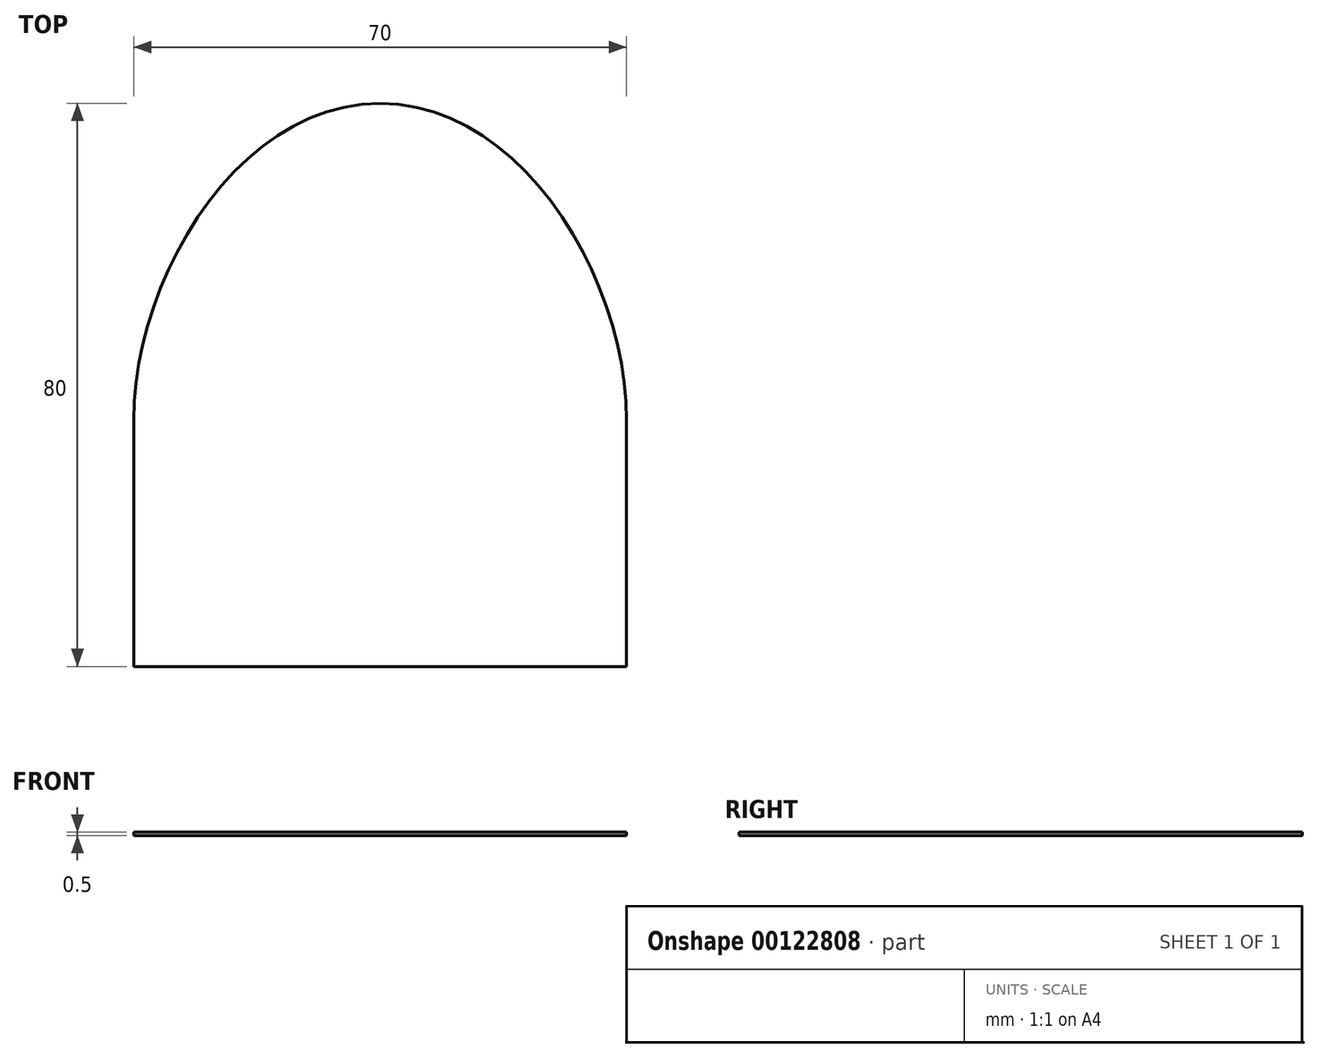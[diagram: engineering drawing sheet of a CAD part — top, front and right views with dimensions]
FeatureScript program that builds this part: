
annotation { "Feature Type Name" : "Feature", "Feature Type Description" : "" }
export const myFeature = defineFeature(function(context is Context, id is Id, definition is map)
    precondition{}
    {
        {
            var Q0;
            Q0=qCreatedBy(makeId("Top.planeOp"),FACE);
            var sketch = newSketch(context, id + "F0", { "sketchPlane" : qUnion([Q0])});
            skLineSegment(sketch, "E0.top", {"start": v(-35, -35) * mm, "end": v(35, -35) * mm});
            skPoint(sketch, "E0.middle", {"position": v(0, 13.14) * mm});
            skPoint(sketch, "E1", {"position": v(0, 0) * mm});
            skCircle(sketch, "E2", {"center": v(0, 0) * mm, "radius": 35 * mm});
            skPoint(sketch, "E3.visualSharp", {"position": v(-35, -35) * mm});
            skPoint(sketch, "E4.visualSharp", {"position": v(35, -35) * mm});
            skPoint(sketch, "E5", {"position": v(-35, 0) * mm});
            skPoint(sketch, "E6", {"position": v(35, 0) * mm});
            skFitSpline(sketch, "E7", {"points": [v(0, 45) * mm, v(-35, 0) * mm], "startDerivative": vector(-60.6, 0) * mm, "endDerivative": vector(0, -60.15) * mm});
            skLineSegment(sketch, "E8", {"start": v(-35, 0) * mm, "end": v(-35, -35) * mm});
            skLineSegment(sketch, "E9", {"start": v(35, 0) * mm, "end": v(35, -35) * mm});
            skFitSpline(sketch, "E10.MirrorCS", {"points": [v(0, 45) * mm, v(35, 0) * mm], "startDerivative": vector(60.6, 0) * mm, "endDerivative": vector(0, -60.15) * mm});
            skFitSpline(sketch, "E11.0", {"points": [v(0, 37) * mm, v(-0.85, 37) * mm, v(-2.51, 36.87) * mm, v(-4.95, 36.3) * mm, v(-7.36, 35.37) * mm, v(-10.54, 33.64) * mm, v(-14.42, 30.55) * mm, v(-18.67, 25.54) * mm, v(-22.24, 19.56) * mm, v(-24.95, 13) * mm, v(-26.62, 6.3) * mm, v(-27, 2.01) * mm, v(-27, 0) * mm]});
            skPoint(sketch, "E12", {"position": v(0, 37) * mm});
            skPoint(sketch, "E13", {"position": v(-7.77, 35.11) * mm});
            skPoint(sketch, "E14", {"position": v(-14.26, 30.43) * mm});
            skPoint(sketch, "E15", {"position": v(-19.34, 24.24) * mm});
            skPoint(sketch, "E16", {"position": v(-23.15, 17.21) * mm});
            skPoint(sketch, "E17", {"position": v(-25.74, 9.64) * mm});
            skLineSegment(sketch, "E18", {"start": v(-27, 0) * mm, "end": v(-27, -35) * mm});
            skPoint(sketch, "E19", {"position": v(-26.96, 1.74) * mm});
            skPoint(sketch, "E20", {"position": v(-27, -6.26) * mm});
            skPoint(sketch, "E21", {"position": v(-27, -14.26) * mm});
            skPoint(sketch, "E22", {"position": v(-27, -22.26) * mm});
            skPoint(sketch, "E23", {"position": v(-27, -30.26) * mm});
            skLineSegment(sketch, "E24.MirrorCS", {"start": v(27, 0) * mm, "end": v(27, -35) * mm});
            skPoint(sketch, "E25.MirrorP", {"position": v(7.77, 35.11) * mm});
            skPoint(sketch, "E26.MirrorP", {"position": v(14.26, 30.43) * mm});
            skPoint(sketch, "E27.MirrorP", {"position": v(19.34, 24.24) * mm});
            skPoint(sketch, "E28.MirrorP", {"position": v(23.15, 17.21) * mm});
            skPoint(sketch, "E29.MirrorP", {"position": v(25.74, 9.64) * mm});
            skPoint(sketch, "E30.MirrorP", {"position": v(26.96, 1.74) * mm});
            skPoint(sketch, "E31.MirrorP", {"position": v(27, -6.26) * mm});
            skPoint(sketch, "E32.MirrorP", {"position": v(27, -14.26) * mm});
            skPoint(sketch, "E33.MirrorP", {"position": v(27, -22.26) * mm});
            skPoint(sketch, "E34.MirrorP", {"position": v(27, -30.26) * mm});
            skFitSpline(sketch, "E35.0", {"points": [v(0, 37) * mm, v(0.85, 37) * mm, v(2.51, 36.87) * mm, v(4.95, 36.3) * mm, v(7.36, 35.37) * mm, v(10.54, 33.64) * mm, v(14.42, 30.55) * mm, v(18.67, 25.54) * mm, v(22.24, 19.56) * mm, v(24.95, 13) * mm, v(26.62, 6.3) * mm, v(27, 2.01) * mm, v(27, 0) * mm]});
            skSolve(sketch);
        }
        {
            var Q0;
            {var subQ0=sQuery(id+"F0.wireOp",EDGE,"E8");Q0=makeQuery(id+"F0.imprint","IMPRINT",FACE,{"disambiguationData":[TD([[makeQuery(id+"F0.imprint","IMPRINT",EDGE,{"derivedFrom":subQ0}),1.0]])]});}
            var Q1;
            {var subQ0=sQuery(id+"F0.wireOp",EDGE,"E18");var subQ1=sQuery(id+"F0.wireOp",EDGE,"E0.top");var subQ2=makeQuery(id+"F0.imprint","INTERSECT",VERTEX,{"derivedFrom":[subQ1,subQ0]});Q1=makeQuery(id+"F0.imprint","IMPRINT",FACE,{"disambiguationData":[TD([[makeQuery(id+"F0.imprint","IMPRINT",EDGE,{"disambiguationData":[TD([[subQ2,-1.0]])],"derivedFrom":subQ1}),1.0]])]});}
            var Q2;
            {var subQ0=sQuery(id+"F0.wireOp",EDGE,"E24.MirrorCS");var subQ1=sQuery(id+"F0.wireOp",EDGE,"E0.top");var subQ2=makeQuery(id+"F0.imprint","INTERSECT",VERTEX,{"derivedFrom":[subQ1,subQ0]});Q2=makeQuery(id+"F0.imprint","IMPRINT",FACE,{"disambiguationData":[TD([[makeQuery(id+"F0.imprint","IMPRINT",EDGE,{"disambiguationData":[TD([[subQ2,1.0]])],"derivedFrom":subQ1}),1.0]])]});}
            var Q3;
            {var subQ0=sQuery(id+"F0.wireOp",EDGE,"E9");Q3=makeQuery(id+"F0.imprint","IMPRINT",FACE,{"disambiguationData":[TD([[makeQuery(id+"F0.imprint","IMPRINT",EDGE,{"derivedFrom":subQ0}),-1.0]])]});}
            var Q4;
            {var subQ1=sQuery(id+"F0.wireOp",EDGE,"E7");Q4=makeQuery(id+"F0.imprint","IMPRINT",FACE,{"disambiguationData":[TD([[makeQuery(id+"F0.imprint","IMPRINT",EDGE,{"derivedFrom":subQ1}),1.0]])]});}
            var Q5;
            {var subQ2=sQuery(id+"F0.wireOp",EDGE,"E35.0");var subQ4=sQuery(id+"F0.wireOp",EDGE,"E24.MirrorCS");var subQ5=makeQuery(id+"F0.imprint","INTERSECT",VERTEX,{"derivedFrom":[subQ4,subQ2]});Q5=makeQuery(id+"F0.imprint","IMPRINT",FACE,{"disambiguationData":[TD([[makeQuery(id+"F0.imprint","IMPRINT",EDGE,{"disambiguationData":[TD([[subQ5,-1.0]])],"derivedFrom":subQ4}),1.0]])]});}
            var Q6;
            {var subQ2=sQuery(id+"F0.wireOp",EDGE,"E11.0");var subQ4=sQuery(id+"F0.wireOp",EDGE,"E18");var subQ6=makeQuery(id+"F0.imprint","INTERSECT",VERTEX,{"derivedFrom":[subQ2,subQ4]});Q6=makeQuery(id+"F0.imprint","IMPRINT",FACE,{"disambiguationData":[TD([[makeQuery(id+"F0.imprint","IMPRINT",EDGE,{"disambiguationData":[TD([[subQ6,1.0]])],"derivedFrom":subQ2}),-1.0]])]});}
            var Q7;
            {var subQ3=sQuery(id+"F0.wireOp",EDGE,"E2");var subQ5=sQuery(id+"F0.wireOp",EDGE,"E35.0");var subQ6=makeQuery(id+"F0.imprint","INTERSECT",VERTEX,{"derivedFrom":[subQ3,subQ5]});Q7=makeQuery(id+"F0.imprint","IMPRINT",FACE,{"disambiguationData":[TD([[makeQuery(id+"F0.imprint","IMPRINT",EDGE,{"disambiguationData":[TD([[subQ6,-1.0]])],"derivedFrom":subQ3}),1.0]])]});}
            var Q8;
            {var subQ0=sQuery(id+"F0.wireOp",EDGE,"E35.0");var subQ1=sQuery(id+"F0.wireOp",EDGE,"E2");var subQ2=makeQuery(id+"F0.imprint","INTERSECT",VERTEX,{"derivedFrom":[subQ1,subQ0]});Q8=makeQuery(id+"F0.imprint","IMPRINT",FACE,{"disambiguationData":[TD([[makeQuery(id+"F0.imprint","IMPRINT",EDGE,{"disambiguationData":[TD([[subQ2,-1.0]])],"derivedFrom":subQ1}),-1.0]])]});}
            extrude(context, id + "F1", {"entities" : qUnion([Q0, Q1, Q2, Q3, Q4, Q5, Q6, Q7, Q8]), "depth" : .5 * mm});
        }
    });
